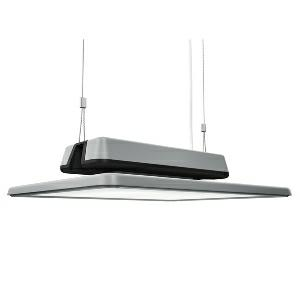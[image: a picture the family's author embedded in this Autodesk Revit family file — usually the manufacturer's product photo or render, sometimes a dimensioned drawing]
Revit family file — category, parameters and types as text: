
# Revit family: acaneo_-_hial_20000_850_w_ea_00734335_6b87
name_source: partatom
category: Lighting Fixtures
units: mm (PartAtom-declared; Revit-internal decimal feet)

## family parameters
Cut with Voids When Loaded = No
Host = Face
Light Source = No
Part Type = Normal
Room Calculation Point = No
Round Connector Dimension = Use Diameter
Shared = No

## types (1)
- ACANEO - HIAL 20000/850/W/EA (1 x LED, 22000 lm, 5000K)
    Apparent Load = 140 VA
    Approval mark = CE
    CIE Flux Codes = 76 97 99 100 100
    Color Rendering = 80-89
    Color Temperature = 5000K
    Control Gear = Electronic ballast
    Default Elevation = 1800 mm
    Description = HIAL 20000/850/W/EA|High bay luminaire|light source: LED|work equipment: Electronic ballast|connected load: 220-240 V, 50/60 Hz|Power consumption: approx. 140 W|power factor: approx. 0,951|luminous flux: 22000 lm|luminous efficacy: 157 lm/W|colour temperature: Cold white, ca. 5000 K|color rendering index (CRI): >= 80|chromaticity tolerance:  3 SDCM|System of protection: IP 65|class of protection: I|technology: Switchable|luminaire body|material: Aluminium|surface: Powder coatet|colour: White aluminium|lamp cover: Acrylic (PMMA), Clear|weight (net): approx. 8.2 kg|mains lead: Built-in plug RST 25i3 Einbau|Fastening: Available separately|Accessory: Junction box (RST 2013)|minimum ambient temperature: -30 ░C|maximum ambient temperature: 50 ░C|glare control: Optics|unified glare rating(4H 8H): <=  25|
    Frequency = 50 Hz, 60 Hz
    Height = 125 mm
    Lamp = 1 x LED
    Lamp Light Flux = 22000 lm
    Lamp count = 1
    Length = 480 mm
    Luminous efficacy = 157 lm/W
    Manufacturer = Waldmann
    ModVariant = No
    Model = 00734335
    Mounting Place = Ceiling
    Mounting Type = Pendant
    Number of Poles = 1
    OnlyDefault = Yes
    Power Factor = 1
    Product Name = ACANEO - HIAL 20000/850/W/EA
    Product group = High bay luminaire (industry)
    ProductGroupID = 901
    Protection Class = Protection class I
    Protection Degree = IP 65
    RLX_Detail_Level = 1
    RLX_Emergency_Light_Flux = 0 lm
    RLX_Emergency_Type = 0
    RLX_Emergency_Type_DB = No
    RlxData = <blob elided: 31173 chars, md5=870d33b2>
    Socket = socket
    Standby Power = 0 W
    System Light Flux = 22000 lm
    System Power = 140 W
    Type Comments = Product without accessories
    Type Image = acaneo-hial.jpg
    URL = http://relux.com
    VarID = ---
    Voltage = 230 V
    Voltage Range = 110-120 V, 220-240 V
    Weight = 0.00 kg
    Width = 405 mm

## geometry (parser evidence)
native form markers: Blend x4, Sweep x11
no freeform markers — native parametric forms only
